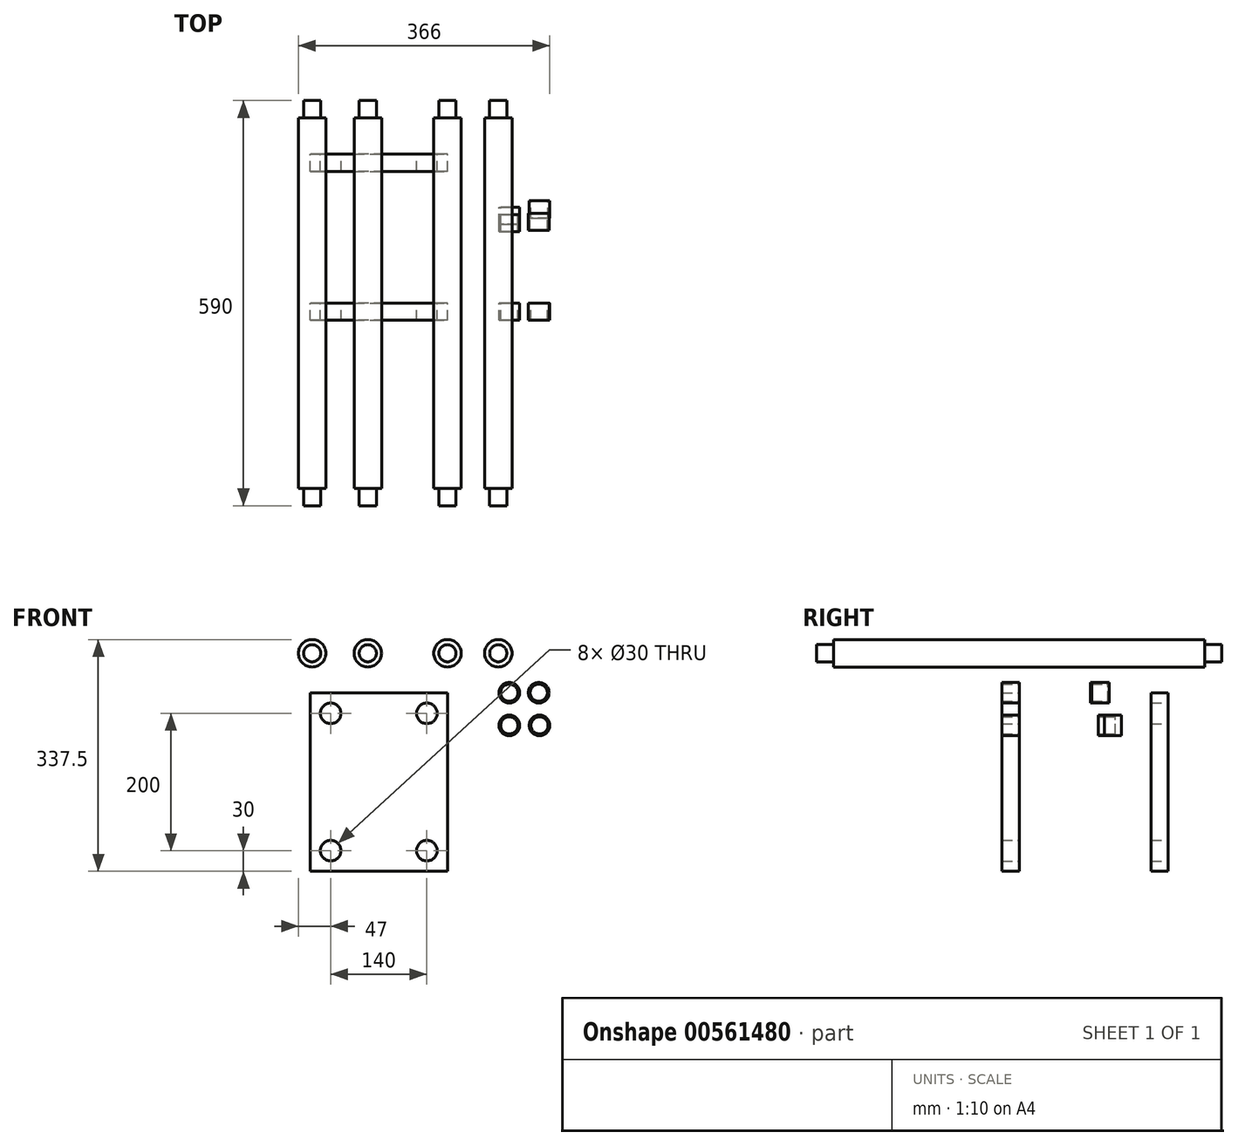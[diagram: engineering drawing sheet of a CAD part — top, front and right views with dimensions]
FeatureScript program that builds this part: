
annotation { "Feature Type Name" : "Feature", "Feature Type Description" : "" }
export const myFeature = defineFeature(function(context is Context, id is Id, definition is map)
    precondition{}
    {
        {
            var Q0;
            Q0=qCreatedBy(makeId("Front.planeOp"),FACE);
            var sketch = newSketch(context, id + "F0", { "sketchPlane" : qUnion([Q0])});
            skLineSegment(sketch, "E0", {"start": v(0, 0) * mm, "end": v(0, -260) * mm});
            skLineSegment(sketch, "E1", {"start": v(0, -260) * mm, "end": v(-200, -260) * mm});
            skLineSegment(sketch, "E2", {"start": v(-200, -260) * mm, "end": v(-200, 0) * mm});
            skCircle(sketch, "E3", {"center": v(-170, -230) * mm, "radius": 15 * mm});
            skCircle(sketch, "E4", {"center": v(-30, -230) * mm, "radius": 15 * mm});
            skCircle(sketch, "E5", {"center": v(-170, -30) * mm, "radius": 15 * mm});
            skCircle(sketch, "E6", {"center": v(-30, -30) * mm, "radius": 15 * mm});
            skLineSegment(sketch, "E7", {"start": v(-200, 0) * mm, "end": v(0, 0) * mm});
            skSolve(sketch);
        }
        {
            var Q0;
            Q0=makeQuery(id+"F0.imprint","IMPRINT",FACE,{"disambiguationData":[TD([[makeQuery(id+"F0.imprint","IMPRINT",EDGE,{"derivedFrom":sQuery(id+"F0.wireOp",EDGE,"E0")}),-1.0]])]});
            extrude(context, id + "F1", {"entities" : qUnion([Q0]), "depth" : 25 * mm, "offsetDistance" : 25 * mm});
        }
        {
            var Q0;
            Q0=qCreatedBy(makeId("Front.planeOp"),FACE);
            var sketch = newSketch(context, id + "F2", { "sketchPlane" : qUnion([Q0])});
            skCircle(sketch, "E8", {"center": v(90, 0) * mm, "radius": 15 * mm});
            skCircle(sketch, "E9", {"center": v(90, 0) * mm, "radius": 12.5 * mm});
            skSolve(sketch);
        }
        {
            var Q0;
            Q0=makeQuery(id+"F2.imprint","IMPRINT",FACE,{"disambiguationData":[TD([[makeQuery(id+"F2.imprint","IMPRINT",EDGE,{"derivedFrom":sQuery(id+"F2.wireOp",EDGE,"E8")}),1.0]])]});
            extrude(context, id + "F3", {"entities" : qUnion([Q0]), "depth" : 25 * mm, "offsetDistance" : 25 * mm});
        }
        {
            var Q0;
            Q0=makeQuery(id+"F3.opExtrude","SWEPT_BODY",BODY,{"disambiguationData":[OSD([sQuery(id+"F2.wireOp",EDGE,"E8"),sQuery(id+"F2.wireOp",EDGE,"E9")])]});
            transform(context, id + "F4", {"entities" : qUnion([Q0]), "transformType" : TransformType.TRANSLATION_3D, "dx" : 42.9 * mm, "dy" : 0 * mm, "dz" : 0 * mm, "makeCopy" : true});
        }
        {
            var Q0;
            Q0=makeQuery(id+"F3.opExtrude","SWEPT_BODY",BODY,{"disambiguationData":[OSD([sQuery(id+"F2.wireOp",EDGE,"E8"),sQuery(id+"F2.wireOp",EDGE,"E9")])]});
            transform(context, id + "F5", {"entities" : qUnion([Q0]), "transformType" : TransformType.TRANSLATION_3D, "dx" : 0 * mm, "dy" : 0 * mm, "dz" : -47.6 * mm, "makeCopy" : true});
        }
        {
            var Q0;
            Q0=makeQuery(id+"F5.opPattern","COPY",BODY,{"derivedFrom":makeQuery(id+"F3.opExtrude","SWEPT_BODY",BODY,{"disambiguationData":[OSD([sQuery(id+"F2.wireOp",EDGE,"E8"),sQuery(id+"F2.wireOp",EDGE,"E9")])]}),"instanceName":"1"});
            transform(context, id + "F6", {"entities" : qUnion([Q0]), "transformType" : TransformType.TRANSLATION_3D, "dx" : 44 * mm, "dy" : 0 * mm, "dz" : 0 * mm, "makeCopy" : true});
        }
        {
            var Q0;
            Q0=makeQuery(id+"F1.opExtrude","SWEPT_BODY",BODY,{"disambiguationData":[OSD([sQuery(id+"F0.wireOp",EDGE,"E0"),sQuery(id+"F0.wireOp",EDGE,"E1"),sQuery(id+"F0.wireOp",EDGE,"E2"),sQuery(id+"F0.wireOp",EDGE,"E3"),sQuery(id+"F0.wireOp",EDGE,"E4"),sQuery(id+"F0.wireOp",EDGE,"E5"),sQuery(id+"F0.wireOp",EDGE,"E6"),sQuery(id+"F0.wireOp",EDGE,"E7")])]});
            transform(context, id + "F7", {"entities" : qUnion([Q0]), "transformType" : TransformType.TRANSLATION_3D, "dx" : 0 * mm, "dy" : 217 * mm, "dz" : 0 * mm, "makeCopy" : true});
        }
        {
            var Q0;
            Q0=makeQuery(id+"F3.opExtrude","SWEPT_BODY",BODY,{"disambiguationData":[OSD([sQuery(id+"F2.wireOp",EDGE,"E8"),sQuery(id+"F2.wireOp",EDGE,"E9")])]});
            transform(context, id + "F8", {"entities" : qUnion([Q0]), "transformType" : TransformType.TRANSLATION_3D, "dx" : 0 * mm, "dy" : 129 * mm, "dz" : 0 * mm, "makeCopy" : true});
        }
        {
            var Q0;
            Q0=makeQuery(id+"F4.opPattern","COPY",BODY,{"derivedFrom":makeQuery(id+"F3.opExtrude","SWEPT_BODY",BODY,{"disambiguationData":[OSD([sQuery(id+"F2.wireOp",EDGE,"E8"),sQuery(id+"F2.wireOp",EDGE,"E9")])]}),"instanceName":"1"});
            transform(context, id + "F9", {"entities" : qUnion([Q0]), "transformType" : TransformType.TRANSLATION_3D, "dx" : 0 * mm, "dy" : 131 * mm, "dz" : 0 * mm, "makeCopy" : true});
        }
        {
            var Q0;
            Q0=makeQuery(id+"F5.opPattern","COPY",BODY,{"derivedFrom":makeQuery(id+"F3.opExtrude","SWEPT_BODY",BODY,{"disambiguationData":[OSD([sQuery(id+"F2.wireOp",EDGE,"E8"),sQuery(id+"F2.wireOp",EDGE,"E9")])]}),"instanceName":"1"});
            transform(context, id + "F10", {"entities" : qUnion([Q0]), "transformType" : TransformType.TRANSLATION_3D, "dx" : 0 * mm, "dy" : 140 * mm, "dz" : 0 * mm, "makeCopy" : true});
        }
        {
            var Q0;
            Q0=makeQuery(id+"F6.opPattern","COPY",BODY,{"derivedFrom":makeQuery(id+"F5.opPattern","COPY",BODY,{"derivedFrom":makeQuery(id+"F3.opExtrude","SWEPT_BODY",BODY,{"disambiguationData":[OSD([sQuery(id+"F2.wireOp",EDGE,"E8"),sQuery(id+"F2.wireOp",EDGE,"E9")])]}),"instanceName":"1"}),"instanceName":"1"});
            transform(context, id + "F11", {"entities" : qUnion([Q0]), "transformType" : TransformType.TRANSLATION_3D, "dx" : 0 * mm, "dy" : 149 * mm, "dz" : 0 * mm, "makeCopy" : true});
        }
        {
            var Q0;
            Q0=qCreatedBy(makeId("Front.planeOp"),FACE);
            var sketch = newSketch(context, id + "F12", { "sketchPlane" : qUnion([Q0])});
            skCircle(sketch, "E10", {"center": v(0, 57.5) * mm, "radius": 20 * mm});
            skCircle(sketch, "E11", {"center": v(0, 57.5) * mm, "radius": 12.5 * mm});
            skSolve(sketch);
        }
        {
            var Q0;
            Q0=makeQuery(id+"F12.imprint","IMPRINT",FACE,{"disambiguationData":[TD([[makeQuery(id+"F12.imprint","IMPRINT",EDGE,{"derivedFrom":sQuery(id+"F12.wireOp",EDGE,"E11")}),1.0]])]});
            extrude(context, id + "F13", {"entities" : qUnion([Q0]), "endBound" : BoundingType.SYMMETRIC, "depth" : 590 * mm, "offsetDistance" : 25 * mm});
        }
        {
            var Q0;
            Q0 = qSketchRegion(id + "F12", true);
            extrude(context, id + "F14", {"entities" : qUnion([Q0]), "operationType" : NewBodyOperationType.ADD, "endBound" : BoundingType.SYMMETRIC, "depth" : 540 * mm, "offsetDistance" : 25 * mm});
        }
        {
            var Q0;
            Q0=makeQuery(id+"F13.opExtrude","SWEPT_BODY",BODY,{"disambiguationData":[OSD([sQuery(id+"F12.wireOp",EDGE,"E11")])]});
            transform(context, id + "F15", {"entities" : qUnion([Q0]), "transformType" : TransformType.TRANSLATION_3D, "dx" : 74 * mm, "dy" : 0 * mm, "dz" : 0 * mm, "makeCopy" : true});
        }
        {
            var Q0;
            Q0=makeQuery(id+"F13.opExtrude","SWEPT_BODY",BODY,{"disambiguationData":[OSD([sQuery(id+"F12.wireOp",EDGE,"E11")])]});
            transform(context, id + "F16", {"entities" : qUnion([Q0]), "transformType" : TransformType.TRANSLATION_3D, "dx" : -116 * mm, "dy" : 0 * mm, "dz" : 0 * mm, "makeCopy" : true});
        }
        {
            var Q0;
            Q0=makeQuery(id+"F16.opPattern","COPY",BODY,{"derivedFrom":makeQuery(id+"F13.opExtrude","SWEPT_BODY",BODY,{"disambiguationData":[OSD([sQuery(id+"F12.wireOp",EDGE,"E11")])]}),"instanceName":"1"});
            transform(context, id + "F17", {"entities" : qUnion([Q0]), "transformType" : TransformType.TRANSLATION_3D, "dx" : -81 * mm, "dy" : 0 * mm, "dz" : 0 * mm, "makeCopy" : true});
        }
    });
